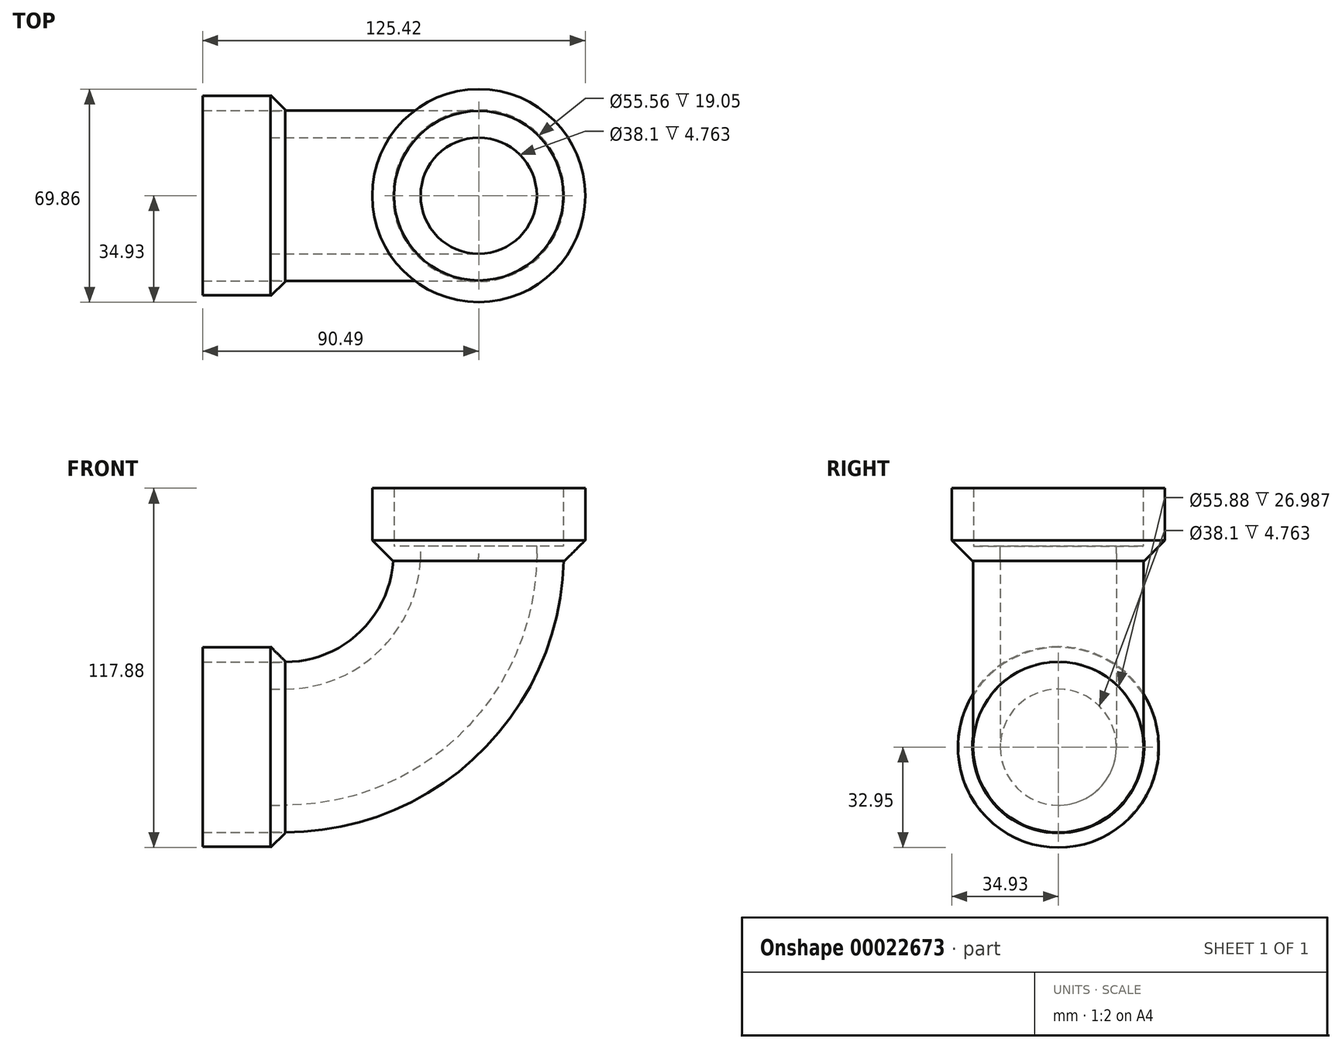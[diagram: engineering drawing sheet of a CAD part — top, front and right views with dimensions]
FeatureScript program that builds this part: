
annotation { "Feature Type Name" : "Feature", "Feature Type Description" : "" }
export const myFeature = defineFeature(function(context is Context, id is Id, definition is map)
    precondition{}
    {
        {
            var Q0;
            Q0=qCreatedBy(makeId("Top.planeOp"),FACE);
            var sketch = newSketch(context, id + "F0", { "sketchPlane" : qUnion([Q0])});
            skCircle(sketch, "E0", {"center": v(0, 0) * mm, "radius": 34.93 * mm});
            skCircle(sketch, "E1", {"center": v(0, 0) * mm, "radius": 27.78 * mm});
            skCircle(sketch, "E2", {"center": v(0, 0) * mm, "radius": 22.23 * mm});
            skSolve(sketch);
        }
        {
            var Q0;
            Q0=makeQuery(id+"F0.imprint","IMPRINT",FACE,{"disambiguationData":[TD([[makeQuery(id+"F0.imprint","IMPRINT",EDGE,{"derivedFrom":sQuery(id+"F0.wireOp",EDGE,"E0")}),1.0]])]});
            extrude(context, id + "F1", {"entities" : qUnion([Q0]), "depth" : 19.05 * mm});
        }
        {
            var Q0;
            Q0=qCreatedBy(makeId("Top.planeOp"),FACE);
            var sketch = newSketch(context, id + "F2", { "sketchPlane" : qUnion([Q0])});
            skCircle(sketch, "E3", {"center": v(0, 0) * mm, "radius": 22.23 * mm});
            skCircle(sketch, "E4", {"center": v(0, 0) * mm, "radius": 34.93 * mm});
            skSolve(sketch);
        }
        {
            var Q0;
            Q0=makeQuery(id+"F2.imprint","IMPRINT",FACE,{"disambiguationData":[TD([[makeQuery(id+"F2.imprint","IMPRINT",EDGE,{"derivedFrom":sQuery(id+"F2.wireOp",EDGE,"E3")}),-1.0]])]});
            extrude(context, id + "F3", {"entities" : qUnion([Q0]), "operationType" : NewBodyOperationType.ADD, "oppositeDirection" : true, "depth" : 4.76 * mm});
        }
        {
            var Q0;
            Q0=makeQuery(id+"F3.opExtrude","CAP_EDGE",EDGE,{"disambiguationData":[OSD([sQuery(id+"F2.wireOp",EDGE,"E4")])],"isStart":false});
            chamfer(context, id + "F4", {"entities" : qUnion([Q0]), "chamferType" : ChamferType.OFFSET_ANGLE, "width" : 6.74 * mm, "oppositeDirection" : false, "angle" : 45 * degree});
        }
        {
            var Q0;
            Q0=qCreatedBy(makeId("Top.planeOp"),FACE);
            var sketch = newSketch(context, id + "F5", { "sketchPlane" : qUnion([Q0])});
            skCircle(sketch, "E5", {"center": v(0, 0) * mm, "radius": 19.05 * mm});
            skCircle(sketch, "E6", {"center": v(0, 0) * mm, "radius": 28.2 * mm});
            skSolve(sketch);
        }
        {
            var Q0;
            Q0=makeQuery(id+"F5.imprint","IMPRINT",FACE,{"disambiguationData":[TD([[makeQuery(id+"F5.imprint","IMPRINT",EDGE,{"derivedFrom":sQuery(id+"F5.wireOp",EDGE,"E5")}),-1.0]])]});
            extrude(context, id + "F6", {"entities" : qUnion([Q0]), "operationType" : NewBodyOperationType.ADD, "oppositeDirection" : true, "depth" : 4.76 * mm});
        }
        {
            var Q0;
            Q0=qCreatedBy(makeId("Top.planeOp"),FACE);
            var sketch = newSketch(context, id + "F7", { "sketchPlane" : qUnion([Q0])});
            skCircle(sketch, "E7", {"center": v(0, 0) * mm, "radius": 19.05 * mm});
            skCircle(sketch, "E8", {"center": v(0, 0) * mm, "radius": 27.94 * mm});
            skSolve(sketch);
        }
        {
            var Q0;
            Q0=qCreatedBy(makeId("Front.planeOp"),FACE);
            var sketch = newSketch(context, id + "F8", { "sketchPlane" : qUnion([Q0])});
            skArc(sketch, "E9", {"start": v(-63.5, -65.88) * mm, "mid": v(-18.6, -47.28) * mm, "end": v(0, -2.38) * mm});
            skLineSegment(sketch, "E10", {"start": v(0, -2.38) * mm, "end": v(0, 0) * mm});
            skSolve(sketch);
        }
        {
            var Q0;
            Q0=qSketchRegion(id+"F7",true);
            var Q1;
            Q1=qConstructionFilter(qBodyType(qCreatedBy(id+"F8",EDGE),BodyType.WIRE),ConstructionObject.NO);
            sweep(context, id + "F9", {"operationType" : NewBodyOperationType.ADD, "profiles" : qUnion([Q0]), "path" : qUnion([Q1])});
        }
        {
            var Q0;
            Q0=makeQuery(id+"F9.opSweep","CAP_FACE",FACE,{"disambiguationData":[OSD([sQuery(id+"F7.wireOp",EDGE,"E7"),sQuery(id+"F7.wireOp",EDGE,"E8"),sQuery(id+"F8.wireOp",VERTEX,"E9.start")])],"isStart":false});
            var sketch = newSketch(context, id + "F10", { "sketchPlane" : qUnion([Q0])});
            skCircle(sketch, "E11", {"center": v(0, -65.88) * mm, "radius": 27.78 * mm});
            skCircle(sketch, "E12", {"center": v(0, -65.88) * mm, "radius": 34.93 * mm});
            skCircle(sketch, "E13", {"center": v(0, -65.88) * mm, "radius": 19.05 * mm});
            skSolve(sketch);
        }
        {
            var Q0;
            Q0=makeQuery(id+"F10.imprint","IMPRINT",FACE,{"disambiguationData":[TD([[makeQuery(id+"F10.imprint","IMPRINT",EDGE,{"derivedFrom":sQuery(id+"F10.wireOp",EDGE,"E12")}),1.0]])]});
            var Q1;
            Q1=makeQuery(id+"F10.imprint","IMPRINT",FACE,{"disambiguationData":[TD([[makeQuery(id+"F10.imprint","IMPRINT",EDGE,{"derivedFrom":sQuery(id+"F10.wireOp",EDGE,"E11")}),1.0]])]});
            extrude(context, id + "F11", {"entities" : qUnion([Q0, Q1]), "operationType" : NewBodyOperationType.ADD, "depth" : 4.76 * mm});
        }
        {
            var Q0;
            Q0=makeQuery(id+"F11.opExtrude","CAP_EDGE",EDGE,{"disambiguationData":[OSD([sQuery(id+"F10.wireOp",EDGE,"E12")])],"isStart":true});
            chamfer(context, id + "F12", {"entities" : qUnion([Q0]), "chamferType" : ChamferType.OFFSET_ANGLE, "width" : 6.74 * mm, "oppositeDirection" : false, "angle" : 45 * degree});
        }
        {
            var Q0;
            Q0=makeQuery(id+"F11.opExtrude","CAP_FACE",FACE,{"disambiguationData":[OSD([sQuery(id+"F7.wireOp",EDGE,"E8"),sQuery(id+"F8.wireOp",VERTEX,"E9.start"),sQuery(id+"F10.wireOp",EDGE,"E12")])],"isStart":false});
            var sketch = newSketch(context, id + "F13", { "sketchPlane" : qUnion([Q0])});
            skCircle(sketch, "E14", {"center": v(0, -65.88) * mm, "radius": 27.75 * mm});
            skCircle(sketch, "E15", {"center": v(0, -65.88) * mm, "radius": 32.7 * mm});
            skSolve(sketch);
        }
        {
            var Q0;
            Q0=makeQuery(id+"F13.imprint","IMPRINT",FACE,{"disambiguationData":[TD([[makeQuery(id+"F13.imprint","IMPRINT",EDGE,{"derivedFrom":sQuery(id+"F13.wireOp",EDGE,"E15")}),1.0]])]});
            extrude(context, id + "F14", {"entities" : qUnion([Q0]), "operationType" : NewBodyOperationType.ADD, "depth" : 22.22 * mm});
        }
    });
